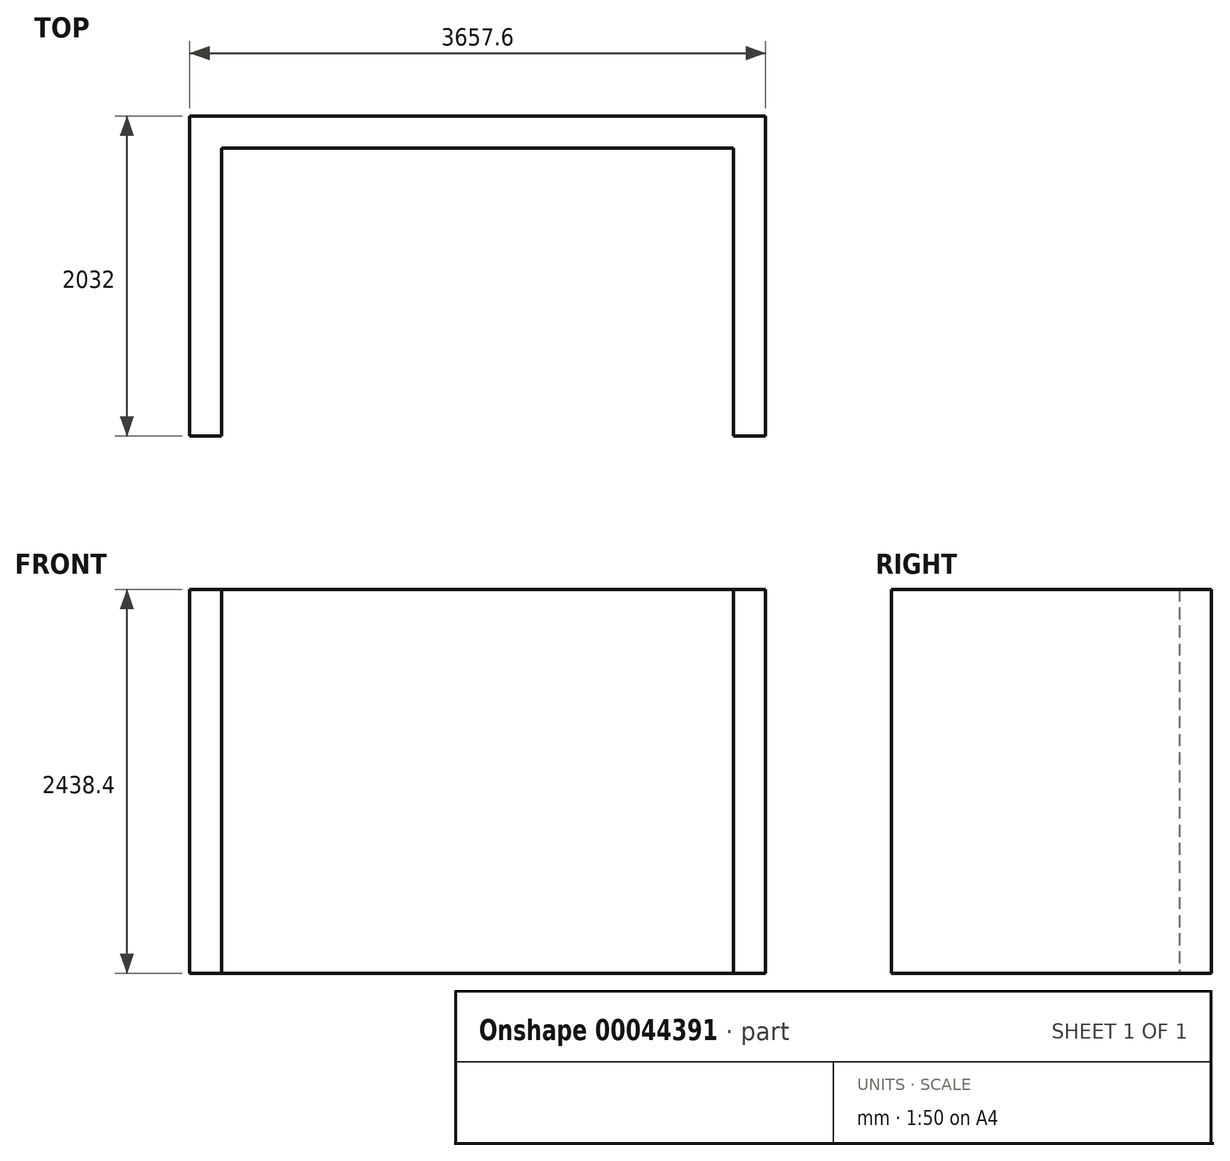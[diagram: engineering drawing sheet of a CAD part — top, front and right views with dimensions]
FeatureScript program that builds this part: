
annotation { "Feature Type Name" : "Feature", "Feature Type Description" : "" }
export const myFeature = defineFeature(function(context is Context, id is Id, definition is map)
    precondition{}
    {
        {
            var Q0;
            Q0=qCreatedBy(makeId("Top.planeOp"),FACE);
            var sketch = newSketch(context, id + "F0", { "sketchPlane" : qUnion([Q0])});
            skLineSegment(sketch, "E0.bottom", {"start": v(-1828.8, -1828.8) * mm, "end": v(-1625.6, -1828.8) * mm});
            skLineSegment(sketch, "E0.left", {"start": v(-1828.8, -1828.8) * mm, "end": v(-1828.8, 203.2) * mm});
            skLineSegment(sketch, "E0.right", {"start": v(-1625.6, -1828.8) * mm, "end": v(-1625.6, 0) * mm});
            skLineSegment(sketch, "E1.top", {"start": v(-1625.6, 0) * mm, "end": v(1625.6, 0) * mm});
            skLineSegment(sketch, "E2.top", {"start": v(1828.8, -1828.8) * mm, "end": v(1625.6, -1828.8) * mm});
            skLineSegment(sketch, "E2.right", {"start": v(1625.6, 0) * mm, "end": v(1625.6, -1828.8) * mm});
            skLineSegment(sketch, "E3", {"start": v(-1828.8, 203.2) * mm, "end": v(1828.8, 203.2) * mm});
            skLineSegment(sketch, "E4", {"start": v(1828.8, 203.2) * mm, "end": v(1828.8, -1828.8) * mm});
            skSolve(sketch);
        }
        {
            var Q0;
            Q0=makeQuery(id+"F0.imprint","IMPRINT",FACE,{"disambiguationData":[TD([[makeQuery(id+"F0.imprint","IMPRINT",EDGE,{"derivedFrom":sQuery(id+"F0.wireOp",EDGE,"E0.bottom")}),1.0]])]});
            extrude(context, id + "F1", {"entities" : qUnion([Q0]), "depth" : 2438.4 * mm});
        }
    });
